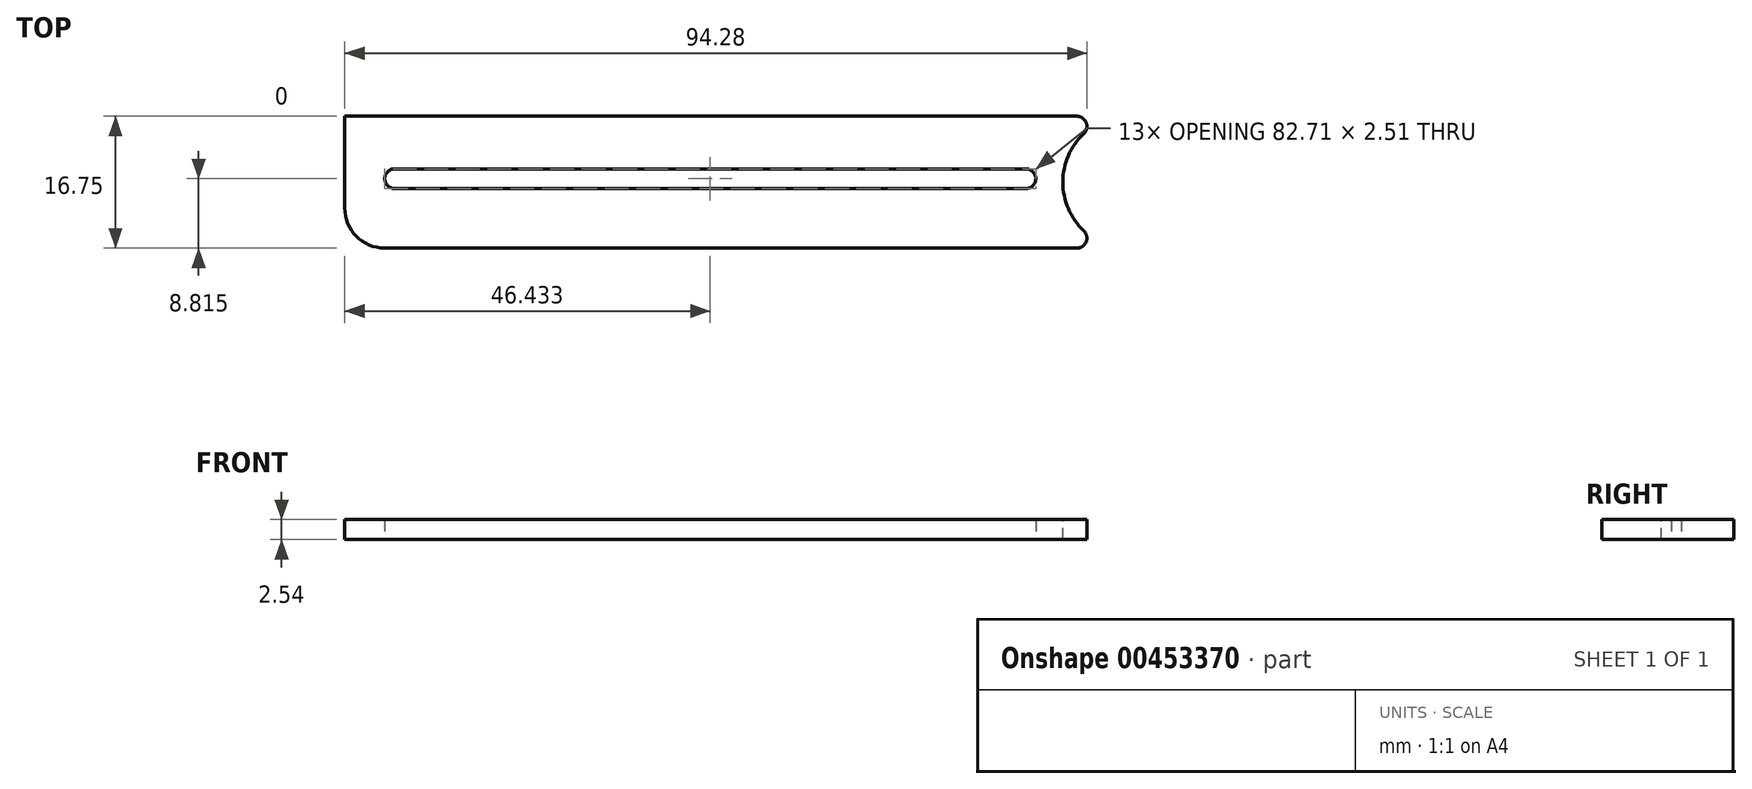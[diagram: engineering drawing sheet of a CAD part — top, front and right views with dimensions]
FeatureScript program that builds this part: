
annotation { "Feature Type Name" : "Feature", "Feature Type Description" : "" }
export const myFeature = defineFeature(function(context is Context, id is Id, definition is map)
    precondition{}
    {
        {
            var Q0;
            Q0=qCreatedBy(makeId("Top.planeOp"),FACE);
            var sketch = newSketch(context, id + "F0", { "sketchPlane" : qUnion([Q0])});
            skLineSegment(sketch, "E0.bottom", {"start": v(-60.97, 0) * mm, "end": v(38.76, 0) * mm});
            skLineSegment(sketch, "E0.top", {"start": v(-60.97, -16.75) * mm, "end": v(38.76, -16.75) * mm});
            skLineSegment(sketch, "E0.left", {"start": v(-60.97, 0) * mm, "end": v(-60.97, -16.75) * mm});
            skLineSegment(sketch, "E0.right", {"start": v(38.76, 0) * mm, "end": v(38.76, -16.75) * mm});
            skSolve(sketch);
        }
        {
            var Q0;
            Q0=makeQuery(id+"F0.imprint","IMPRINT",FACE,{"disambiguationData":[TD([[makeQuery(id+"F0.imprint","IMPRINT",EDGE,{"derivedFrom":sQuery(id+"F0.wireOp",EDGE,"E0.bottom")}),-1.0]])]});
            extrude(context, id + "F1", {"entities" : qUnion([Q0]), "depth" : 2.54 * mm});
        }
        {
            var Q0;
            Q0=makeQuery(id+"F1.opExtrude","SWEPT_EDGE",EDGE,{"disambiguationData":[OSD([sQuery(id+"F0.wireOp",EDGE,"E0.top"),sQuery(id+"F0.wireOp",EDGE,"E0.left")])]});
            fillet(context, id + "F2", {"entities" : qUnion([Q0]), "radius" : 5.08 * mm, "tangentPropagation" : true, "allowEdgeOverflow" : false});
        }
        {
            var Q0;
            Q0=makeQuery(id+"F1.opExtrude","CAP_FACE",FACE,{"disambiguationData":[OSD([sQuery(id+"F0.wireOp",EDGE,"E0.bottom"),sQuery(id+"F0.wireOp",EDGE,"E0.top"),sQuery(id+"F0.wireOp",EDGE,"E0.left"),sQuery(id+"F0.wireOp",EDGE,"E0.right")])],"isStart":false});
            var sketch = newSketch(context, id + "F3", { "sketchPlane" : qUnion([Q0])});
            skCircle(sketch, "E1", {"center": v(38.76, -8.37) * mm, "radius": 8.5 * mm});
            skSolve(sketch);
        }
        {
            var Q0;
            Q0 = qSketchRegion(id + "F3", true);
            extrude(context, id + "F4", {"entities" : qUnion([Q0]), "operationType" : NewBodyOperationType.REMOVE, "oppositeDirection" : true, "depth" : 2.54 * mm});
        }
        {
            var Q0;
            Q0=makeQuery(id+"F1.opExtrude","CAP_FACE",FACE,{"disambiguationData":[OSD([sQuery(id+"F0.wireOp",EDGE,"E0.bottom"),sQuery(id+"F0.wireOp",EDGE,"E0.top"),sQuery(id+"F0.wireOp",EDGE,"E0.left"),sQuery(id+"F0.wireOp",EDGE,"E0.right")])],"isStart":true});
            var sketch = newSketch(context, id + "F5", { "sketchPlane" : qUnion([Q0])});
            skLineSegment(sketch, "E2.bottom", {"start": v(-55.89, 9.2) * mm, "end": v(26.82, 9.2) * mm});
            skLineSegment(sketch, "E2.top", {"start": v(-55.89, 6.68) * mm, "end": v(26.82, 6.68) * mm});
            skLineSegment(sketch, "E2.left", {"start": v(-55.89, 9.2) * mm, "end": v(-55.89, 6.68) * mm});
            skLineSegment(sketch, "E2.right", {"start": v(26.82, 9.2) * mm, "end": v(26.82, 6.68) * mm});
            skSolve(sketch);
        }
        {
            var Q0;
            Q0 = qSketchRegion(id + "F5", true);
            extrude(context, id + "F6", {"entities" : qUnion([Q0]), "operationType" : NewBodyOperationType.REMOVE, "oppositeDirection" : true, "depth" : 2.54 * mm});
        }
        {
            var Q0;
            Q0=makeQuery(id+"F6.boolean.opBoolean","COPY",EDGE,{"derivedFrom":makeQuery(id+"F6.opExtrude","SWEPT_EDGE",EDGE,{"disambiguationData":[OSD([sQuery(id+"F5.wireOp",EDGE,"E2.bottom"),sQuery(id+"F5.wireOp",EDGE,"E2.left")])]})});
            fillet(context, id + "F7", {"entities" : qUnion([Q0]), "radius" : 1.27 * mm, "tangentPropagation" : true, "allowEdgeOverflow" : false});
        }
        {
            var Q0;
            Q0=makeQuery(id+"F6.boolean.opBoolean","COPY",EDGE,{"derivedFrom":makeQuery(id+"F6.opExtrude","SWEPT_EDGE",EDGE,{"disambiguationData":[OSD([sQuery(id+"F5.wireOp",EDGE,"E2.top"),sQuery(id+"F5.wireOp",EDGE,"E2.left")])]})});
            fillet(context, id + "F8", {"entities" : qUnion([Q0]), "radius" : 1.27 * mm, "tangentPropagation" : true, "allowEdgeOverflow" : false});
        }
        {
            var Q0;
            Q0=makeQuery(id+"F6.boolean.opBoolean","COPY",EDGE,{"derivedFrom":makeQuery(id+"F6.opExtrude","SWEPT_EDGE",EDGE,{"disambiguationData":[OSD([sQuery(id+"F5.wireOp",EDGE,"E2.top"),sQuery(id+"F5.wireOp",EDGE,"E2.right")])]})});
            fillet(context, id + "F9", {"entities" : qUnion([Q0]), "radius" : 1.27 * mm, "tangentPropagation" : true, "allowEdgeOverflow" : false});
        }
        {
            var Q0;
            Q0=makeQuery(id+"F6.boolean.opBoolean","COPY",EDGE,{"derivedFrom":makeQuery(id+"F6.opExtrude","SWEPT_EDGE",EDGE,{"disambiguationData":[OSD([sQuery(id+"F5.wireOp",EDGE,"E2.bottom"),sQuery(id+"F5.wireOp",EDGE,"E2.right")])]})});
            fillet(context, id + "F10", {"entities" : qUnion([Q0]), "radius" : 1.27 * mm, "tangentPropagation" : true, "allowEdgeOverflow" : false});
        }
        {
            var Q0;
            Q0=makeQuery(id+"F4.boolean.opBoolean","INTERSECT",EDGE,{"derivedFrom":[makeQuery(id+"F1.opExtrude","SWEPT_FACE",FACE,{"disambiguationData":[OSD([sQuery(id+"F0.wireOp",EDGE,"E0.top")])]}),makeQuery(id+"F4.opExtrude","SWEPT_FACE",FACE,{"disambiguationData":[OSD([sQuery(id+"F3.wireOp",EDGE,"E1")])]})]});
            fillet(context, id + "F11", {"entities" : qUnion([Q0]), "radius" : 1.27 * mm, "tangentPropagation" : true, "allowEdgeOverflow" : false});
        }
        {
            var Q0;
            Q0=makeQuery(id+"F4.boolean.opBoolean","INTERSECT",EDGE,{"derivedFrom":[makeQuery(id+"F1.opExtrude","SWEPT_FACE",FACE,{"disambiguationData":[OSD([sQuery(id+"F0.wireOp",EDGE,"E0.bottom")])]}),makeQuery(id+"F4.opExtrude","SWEPT_FACE",FACE,{"disambiguationData":[OSD([sQuery(id+"F3.wireOp",EDGE,"E1")])]})]});
            fillet(context, id + "F12", {"entities" : qUnion([Q0]), "radius" : 1.27 * mm, "tangentPropagation" : true, "allowEdgeOverflow" : false});
        }
    });
